# Revit family: Electronics_Visual-TVs_ViewSonic_ViewSonicR-IFP6570-8670-ViewBoard-Interactive-Flat-Panel
name_source: partatom
category: Electrical Equipment
revit_build: Autodesk Revit 2017 (Build: 20171027_0315(x64)
units: mm (PartAtom-declared; Revit-internal decimal feet)

## family parameters
Always vertical = Yes
Cut with Voids When Loaded = No
OmniClass Number = 23.85.10.14.24.17
OmniClass Title = Plasma Video Monitors
Panel Configuration = Two Columns, Circuits Across
Part Type = Panelboard
Room Calculation Point = No
Round Connector Dimension = Use Diameter
Shared = No
Work Plane-Based = No

## types (2) — shared parameters
Aspect Ratio = 16:9
Assembly Code = D5030500
Backlight Life = 30,000 Hours (Min)
Bezel = Slim
Brightness = 350 nits (typ.)
Colors = 1.07B (10bit)
Contrast Ratio = 1200:1 Typ.
Cover Material = Plastic - ViewSonic - Black
Edition number = 1
Keynote = 11130
Manufacturer = ViewSonic
Native Resolution = UHD 3840x2160(Pixels)
Orientation = Landscape
Product data url = https://www.bimobject.com
Response Time = 8ms
Surface Treatment = Anti-Glare/anti finger print
Type/ Tech = TFT LCD Module with DLED Backlight
URL = https://www.viewsonic.com
Viewing Angles = H = 178, V = 178 typ.

## per-type parameters (varying)
| type | Description | Display Area (mm) | IFP6570 | IFP8670 | Model | Panel Size | Product Guid | Screen Material |
| IFP 6570 | From executive boardrooms to kindergarten classrooms, the ViewSonic® ViewBoard® IFP6570 enables limitless collaboration and endless innovation. Designed to help teams connect, collaborate, and create, this next-generation digital whiteboard delivers exactly what you need to move your ideas forward. A premium, state-of-the-art design features a bezel-less PCAP (projected capacitive) touchscreen with incredible 4K Ultra HD resolution. This highly accurate interactive screen provides for an incredibly natural and responsive handwriting experience. Using fingers, styluses, or both, multiple users can simultaneously write or draw on the huge 65” ViewBoard panel. What’s more, meetings and presentations start fast thanks to convenient one-wire USB-C connectivity. | 1428.48(H) x 803.52(V) mm (64.5” diagonal) | Yes | No | viewsonic_ifp6570 | 65" | 0e85d141-102a-484e-8f34-a685a385ac3e | Screen - ViewSonic - IFP6570 |
| IFP 8670 | From executive boardrooms to kindergarten classrooms, the ViewSonic® ViewBoard® IFP8670 enables limitless collaboration and endless innovation. Designed to help teams connect, collaborate, and create, this next-generation digital whiteboard delivers exactly what you need to move your ideas forward. A premium, state-of-the-art design features a bezel-less PCAP (projected capacitive) touchscreen with incredible 4K Ultra HD resolution. This highly accurate interactive screen provides for an incredibly natural and responsive handwriting experience. Using fingers, styluses, or both, multiple users can simultaneously write or draw on the huge 86” ViewBoard panel. What’s more, meetings and presentations start fast thanks to convenient one-wire USB-C connectivity. | 1895.04 (H) x 1065.96 (V) (85.6”diagonal) | No | Yes | viewsonic_ifp8670 | 86" | 8159dfac-f8ee-4751-a0b7-b4e89c10934e | Screen - ViewSonic - IFP8670 |

## geometry (parser evidence)
native form markers: Sweep x6
no freeform markers — native parametric forms only
